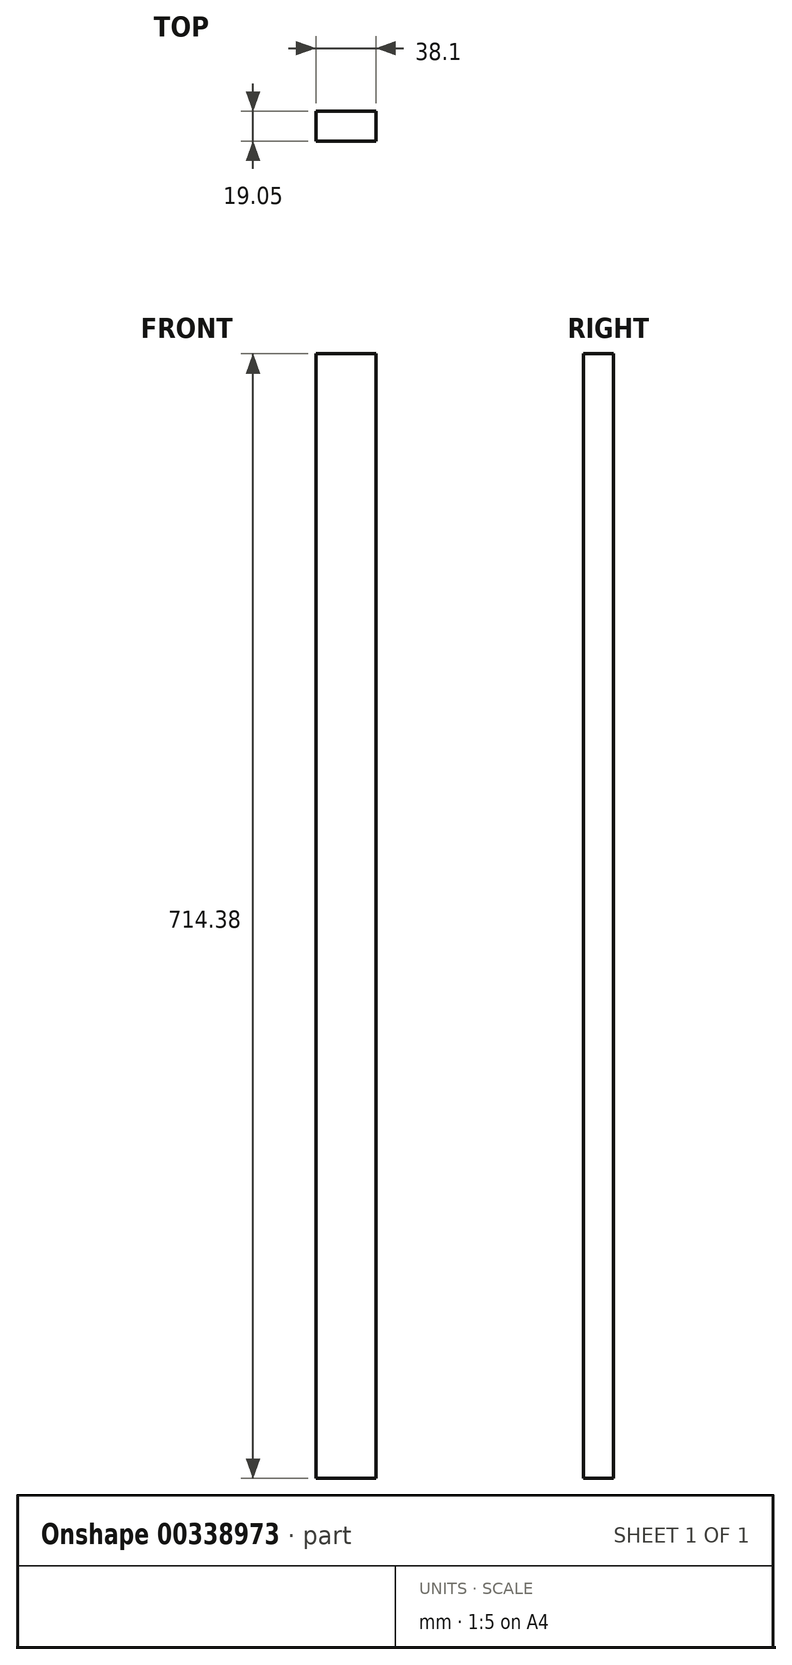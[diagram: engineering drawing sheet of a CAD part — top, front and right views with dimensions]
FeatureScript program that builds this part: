
annotation { "Feature Type Name" : "Feature", "Feature Type Description" : "" }
export const myFeature = defineFeature(function(context is Context, id is Id, definition is map)
    precondition{}
    {
        {
            var Q0;
            Q0=qCreatedBy(makeId("Front.planeOp"),FACE);
            var sketch = newSketch(context, id + "F0", { "sketchPlane" : qUnion([Q0])});
            skLineSegment(sketch, "E0.bottom", {"start": v(19.05, -357.19) * mm, "end": v(-19.05, -357.19) * mm});
            skLineSegment(sketch, "E0.top", {"start": v(19.05, 357.19) * mm, "end": v(-19.05, 357.19) * mm});
            skLineSegment(sketch, "E0.left", {"start": v(19.05, -357.19) * mm, "end": v(19.05, 357.19) * mm});
            skLineSegment(sketch, "E0.right", {"start": v(-19.05, -357.19) * mm, "end": v(-19.05, 357.19) * mm});
            skPoint(sketch, "E0.middle", {"position": v(0, 0) * mm});
            skSolve(sketch);
        }
        {
            var Q0;
            Q0 = qSketchRegion(id + "F0", true);
            extrude(context, id + "F1", {"entities" : qUnion([Q0]), "depth" : 19.05 * mm});
        }
    });
